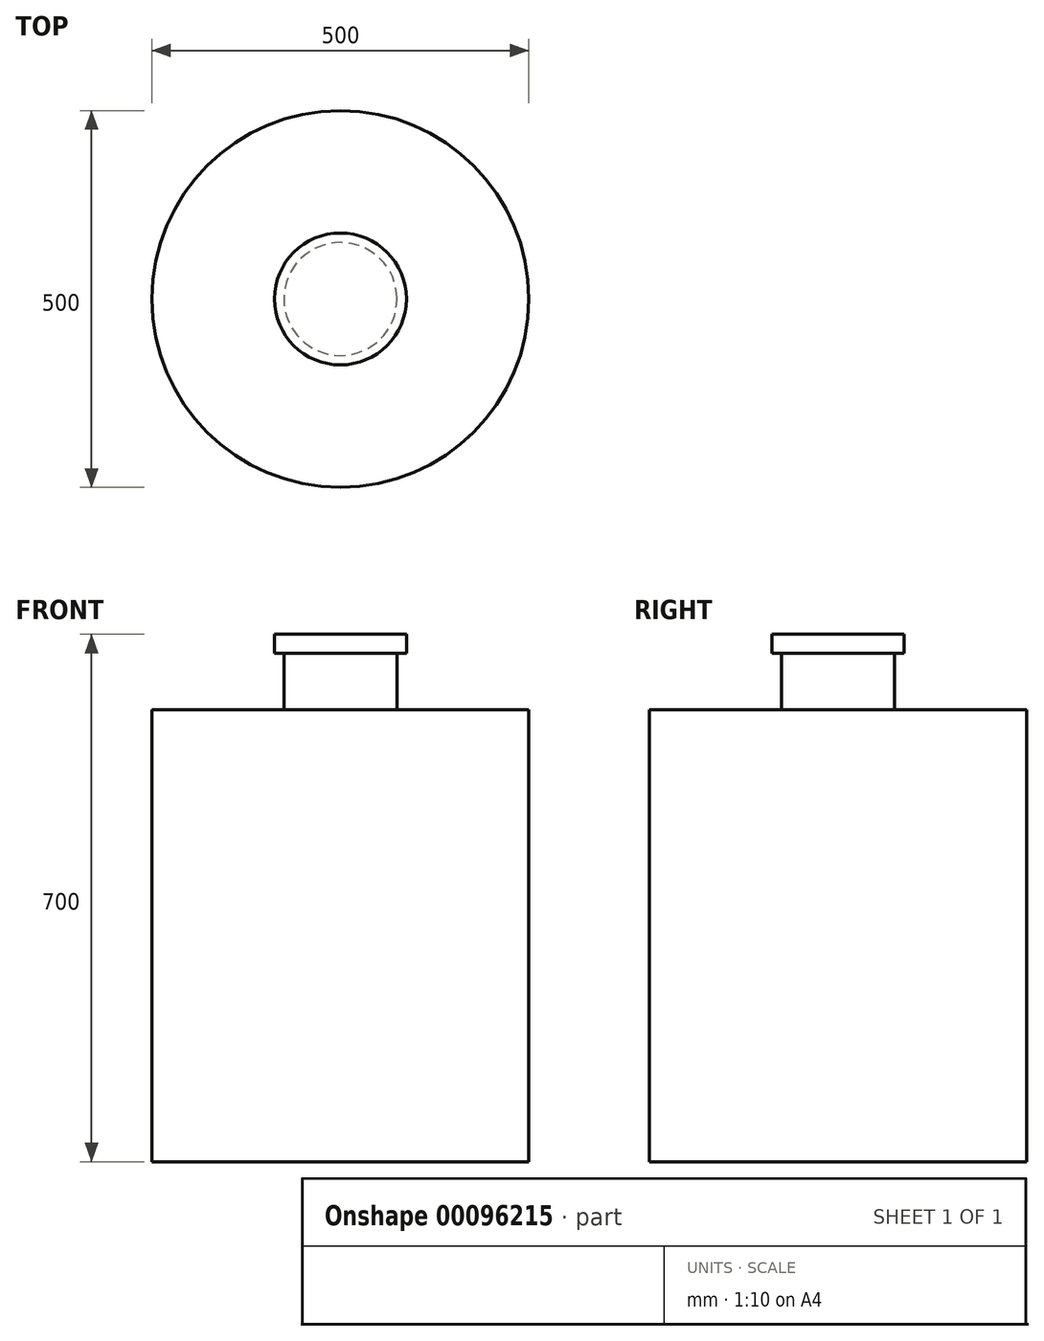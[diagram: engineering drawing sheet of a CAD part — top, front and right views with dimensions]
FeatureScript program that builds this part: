
annotation { "Feature Type Name" : "Feature", "Feature Type Description" : "" }
export const myFeature = defineFeature(function(context is Context, id is Id, definition is map)
    precondition{}
    {
        {
            var Q0;
            Q0=qCreatedBy(makeId("Front.planeOp"),FACE);
            var sketch = newSketch(context, id + "F0", { "sketchPlane" : qUnion([Q0])});
            skLineSegment(sketch, "E0.bottom", {"start": v(250, 300) * mm, "end": v(-250, 300) * mm});
            skLineSegment(sketch, "E0.top", {"start": v(250, -300) * mm, "end": v(-250, -300) * mm});
            skLineSegment(sketch, "E0.left", {"start": v(250, 300) * mm, "end": v(250, -300) * mm});
            skLineSegment(sketch, "E0.right", {"start": v(-250, 300) * mm, "end": v(-250, -300) * mm});
            skPoint(sketch, "E0.middle", {"position": v(0, 0) * mm});
            skLineSegment(sketch, "E1", {"start": v(0, 300) * mm, "end": v(0, -300) * mm});
            skLineSegment(sketch, "E2.bottom", {"start": v(0, -201.17) * mm, "end": v(420, -201.17) * mm});
            skLineSegment(sketch, "E2.top", {"start": v(0, -126.17) * mm, "end": v(420, -126.17) * mm});
            skLineSegment(sketch, "E2.left", {"start": v(0, -201.17) * mm, "end": v(0, -126.17) * mm});
            skLineSegment(sketch, "E2.right", {"start": v(420, -201.17) * mm, "end": v(420, -126.17) * mm});
            skSolve(sketch);
        }
        {
            var Q0;
            {var subQ0=sQuery(id+"F0.wireOp",EDGE,"E0.left");Q0=makeQuery(id+"F0.imprint","IMPRINT",FACE,{"disambiguationData":[TD([[makeQuery(id+"F0.imprint","IMPRINT",EDGE,{"derivedFrom":subQ0}),-1.0]])]});}
            var Q1;
            Q1=sQuery(id+"F0.wireOp",EDGE,"E1");
            revolve(context, id + "F1", {"entities" : qUnion([Q0]), "axis" : qUnion([Q1]), "revolveType" : RevolveType.FULL});
        }
        {
            var Q0;
            Q0=makeQuery(id+"F1.opRevolve","SWEPT_FACE",FACE,{"disambiguationData":[OSD([sQuery(id+"F0.wireOp",EDGE,"E0.bottom")])]});
            var sketch = newSketch(context, id + "F2", { "sketchPlane" : qUnion([Q0])});
            skCircle(sketch, "E3", {"center": v(0, 0) * mm, "radius": 75 * mm});
            skSolve(sketch);
        }
        {
            var Q0;
            Q0 = qSketchRegion(id + "F2", true);
            extrude(context, id + "F3", {"entities" : qUnion([Q0]), "operationType" : NewBodyOperationType.ADD, "depth" : 100 * mm});
        }
        {
            var Q0;
            Q0=makeQuery(id+"F3.opExtrude","CAP_FACE",FACE,{"disambiguationData":[OSD([sQuery(id+"F2.wireOp",EDGE,"E3")])],"isStart":false});
            var sketch = newSketch(context, id + "F4", { "sketchPlane" : qUnion([Q0])});
            skCircle(sketch, "E4", {"center": v(0, 0) * mm, "radius": 87.5 * mm});
            skSolve(sketch);
        }
        {
            var Q0;
            Q0 = qSketchRegion(id + "F4", true);
            extrude(context, id + "F5", {"entities" : qUnion([Q0]), "operationType" : NewBodyOperationType.ADD, "oppositeDirection" : true, "depth" : 25 * mm});
        }
        {
            var Q0;
            {var subQ5=sQuery(id+"F0.wireOp",EDGE,"E2.right");Q0=makeQuery(id+"F0.imprint","IMPRINT",FACE,{"disambiguationData":[TD([[makeQuery(id+"F0.imprint","IMPRINT",EDGE,{"derivedFrom":subQ5}),1.0]])]});}
            var Q1;
            Q1=sQuery(id+"F0.wireOp",EDGE,"E2.top");
            revolve(context, id + "F6", {"operationType" : NewBodyOperationType.ADD, "entities" : qUnion([Q0]), "axis" : qUnion([Q1]), "revolveType" : RevolveType.FULL});
        }
        {
            var Q0;
            Q0=makeQuery(id+"F6.opRevolve","SWEPT_FACE",FACE,{"disambiguationData":[OSD([sQuery(id+"F0.wireOp",EDGE,"E2.right")])]});
            var sketch = newSketch(context, id + "F7", { "sketchPlane" : qUnion([Q0])});
            skCircle(sketch, "E5", {"center": v(0, -126.17) * mm, "radius": 87.5 * mm});
            skSolve(sketch);
        }
        {
            var Q0;
            Q0 = qSketchRegion(id + "F7", true);
            extrude(context, id + "F8", {"entities" : qUnion([Q0]), "operationType" : NewBodyOperationType.ADD, "oppositeDirection" : true, "depth" : 25 * mm});
        }
        {
            var Q0;
            Q0=makeQuery(id+"F6.opRevolve","SWEPT_BODY",BODY,{"disambiguationData":[OSD([sQuery(id+"F0.wireOp",EDGE,"E0.left"),sQuery(id+"F0.wireOp",EDGE,"E2.bottom"),sQuery(id+"F0.wireOp",EDGE,"E2.top"),sQuery(id+"F0.wireOp",EDGE,"E2.right")])]});
            transform(context, id + "F9", {"entities" : qUnion([Q0]), "transformType" : TransformType.TRANSLATION_3D, "dx" : 0 * mm, "dy" : 0 * mm, "dz" : 0 * mm, "makeCopy" : true});
        }
        {
            var Q0;
            Q0=makeQuery(id+"F6.opRevolve","SWEPT_BODY",BODY,{"disambiguationData":[OSD([sQuery(id+"F0.wireOp",EDGE,"E0.left"),sQuery(id+"F0.wireOp",EDGE,"E2.bottom"),sQuery(id+"F0.wireOp",EDGE,"E2.top"),sQuery(id+"F0.wireOp",EDGE,"E2.right")])]});
            deleteBodies(context, id + "F10", {"entities" : qUnion([Q0])});
        }
        {
            var Q0;
            Q0=makeQuery(id+"F9.opPattern","COPY",BODY,{"derivedFrom":makeQuery(id+"F6.opRevolve","SWEPT_BODY",BODY,{"disambiguationData":[OSD([sQuery(id+"F0.wireOp",EDGE,"E0.left"),sQuery(id+"F0.wireOp",EDGE,"E2.bottom"),sQuery(id+"F0.wireOp",EDGE,"E2.top"),sQuery(id+"F0.wireOp",EDGE,"E2.right")])]}),"instanceName":"1"});
            deleteBodies(context, id + "F11", {"entities" : qUnion([Q0])});
        }
    });
